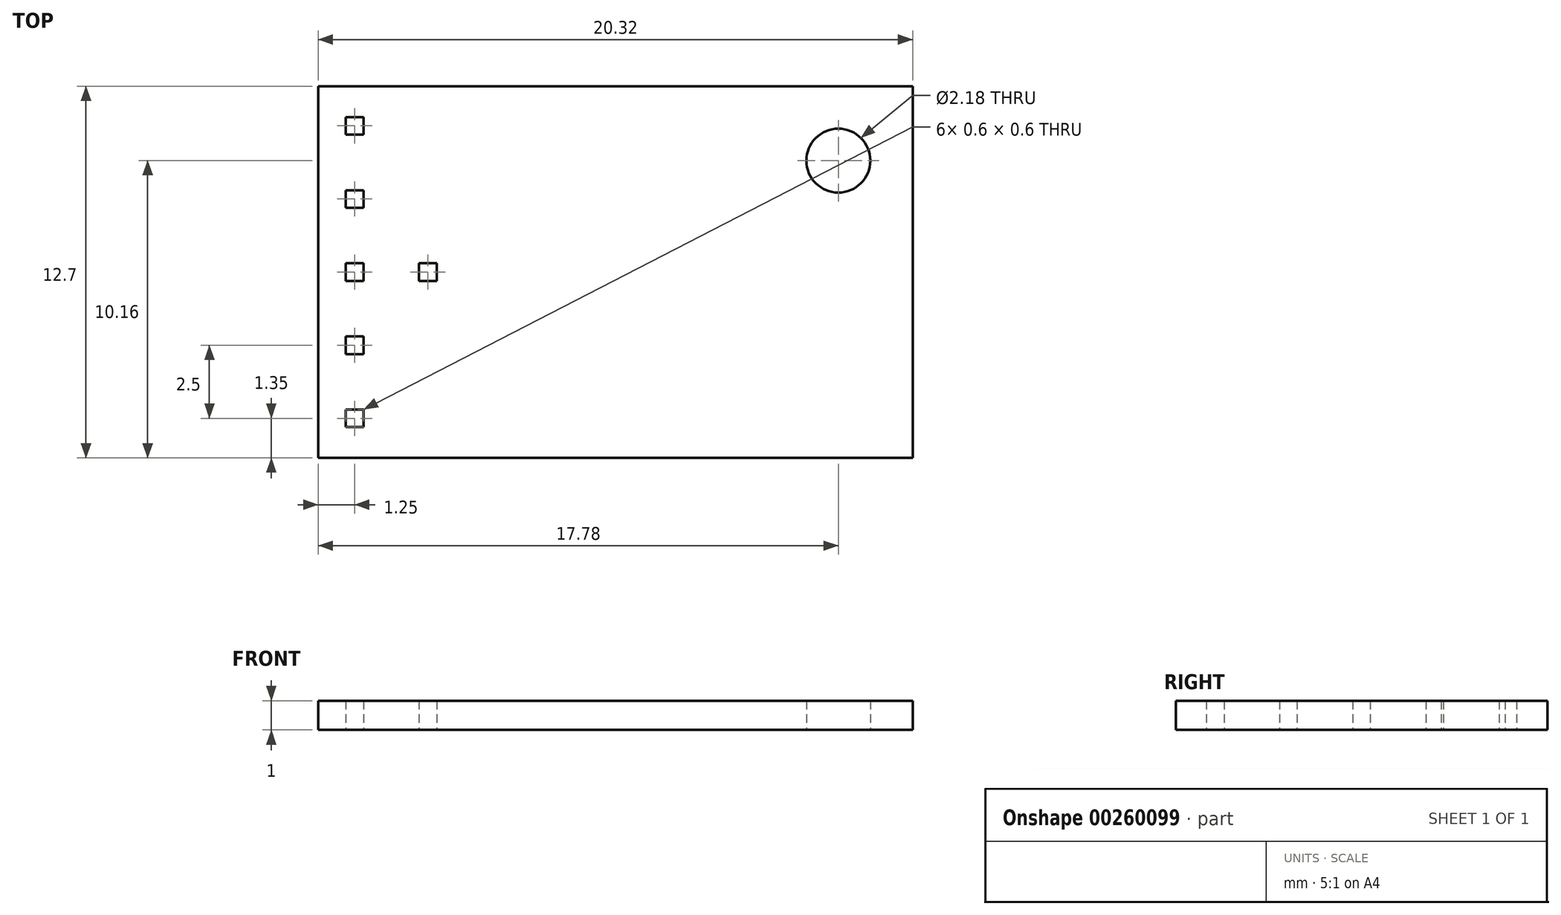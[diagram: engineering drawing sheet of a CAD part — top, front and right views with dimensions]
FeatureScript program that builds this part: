
annotation { "Feature Type Name" : "Feature", "Feature Type Description" : "" }
export const myFeature = defineFeature(function(context is Context, id is Id, definition is map)
    precondition{}
    {
        {
            var Q0;
            Q0=qCreatedBy(makeId("Top.planeOp"),FACE);
            var sketch = newSketch(context, id + "F0", { "sketchPlane" : qUnion([Q0])});
            skLineSegment(sketch, "E0.bottom", {"start": v(0, 0) * mm, "end": v(20.32, 0) * mm});
            skLineSegment(sketch, "E0.top", {"start": v(0, 12.7) * mm, "end": v(20.32, 12.7) * mm});
            skLineSegment(sketch, "E0.left", {"start": v(0, 0) * mm, "end": v(0, 12.7) * mm});
            skLineSegment(sketch, "E0.right", {"start": v(20.32, 0) * mm, "end": v(20.32, 12.7) * mm});
            skCircle(sketch, "E1", {"center": v(17.78, 10.16) * mm, "radius": 1.1 * mm});
            skLineSegment(sketch, "E2", {"start": v(1.25, 12.7) * mm, "end": v(1.25, 0) * mm, "construction": true});
            skLineSegment(sketch, "E3", {"start": v(0, 6.35) * mm, "end": v(20.32, 6.35) * mm, "construction": true});
            skLineSegment(sketch, "E4.bottom", {"start": v(0.95, 6.65) * mm, "end": v(1.55, 6.65) * mm});
            skLineSegment(sketch, "E4.top", {"start": v(0.95, 6.05) * mm, "end": v(1.55, 6.05) * mm});
            skLineSegment(sketch, "E4.left", {"start": v(0.95, 6.65) * mm, "end": v(0.95, 6.05) * mm});
            skLineSegment(sketch, "E4.right", {"start": v(1.55, 6.65) * mm, "end": v(1.55, 6.05) * mm});
            skLineSegment(sketch, "E5.1.0.0", {"start": v(1.55, 9.15) * mm, "end": v(1.55, 8.55) * mm});
            skLineSegment(sketch, "E5.1.0.1", {"start": v(0.95, 9.15) * mm, "end": v(1.55, 9.15) * mm});
            skLineSegment(sketch, "E5.1.0.2", {"start": v(0.95, 9.15) * mm, "end": v(0.95, 8.55) * mm});
            skLineSegment(sketch, "E5.1.0.3", {"start": v(0.95, 8.55) * mm, "end": v(1.55, 8.55) * mm});
            skLineSegment(sketch, "E5.2.0.0", {"start": v(1.55, 11.65) * mm, "end": v(1.55, 11.05) * mm});
            skLineSegment(sketch, "E5.2.0.1", {"start": v(0.95, 11.65) * mm, "end": v(1.55, 11.65) * mm});
            skLineSegment(sketch, "E5.2.0.2", {"start": v(0.95, 11.65) * mm, "end": v(0.95, 11.05) * mm});
            skLineSegment(sketch, "E5.2.0.3", {"start": v(0.95, 11.05) * mm, "end": v(1.55, 11.05) * mm});
            skLineSegment(sketch, "E5.direction1", {"start": v(1.55, 6.05) * mm, "end": v(1.55, 8.55) * mm, "construction": true});
            skLineSegment(sketch, "E6.1.0.0", {"start": v(0.95, 4.15) * mm, "end": v(1.55, 4.15) * mm});
            skLineSegment(sketch, "E6.1.0.1", {"start": v(0.95, 4.15) * mm, "end": v(0.95, 3.55) * mm});
            skLineSegment(sketch, "E6.1.0.2", {"start": v(0.95, 3.55) * mm, "end": v(1.55, 3.55) * mm});
            skLineSegment(sketch, "E6.2.0.0", {"start": v(0.95, 1.65) * mm, "end": v(1.55, 1.65) * mm});
            skLineSegment(sketch, "E6.2.0.1", {"start": v(0.95, 1.65) * mm, "end": v(0.95, 1.05) * mm});
            skLineSegment(sketch, "E6.2.0.2", {"start": v(0.95, 1.05) * mm, "end": v(1.55, 1.05) * mm});
            skLineSegment(sketch, "E6.direction1", {"start": v(0.95, 6.65) * mm, "end": v(0.95, 4.15) * mm, "construction": true});
            skLineSegment(sketch, "E7", {"start": v(1.55, 4.15) * mm, "end": v(1.55, 3.55) * mm});
            skLineSegment(sketch, "E8", {"start": v(1.55, 1.65) * mm, "end": v(1.55, 1.05) * mm});
            skLineSegment(sketch, "E9.bottom", {"start": v(3.45, 6.65) * mm, "end": v(4.05, 6.65) * mm});
            skLineSegment(sketch, "E9.top", {"start": v(3.45, 6.05) * mm, "end": v(4.05, 6.05) * mm});
            skLineSegment(sketch, "E9.left", {"start": v(3.45, 6.65) * mm, "end": v(3.45, 6.05) * mm});
            skLineSegment(sketch, "E9.right", {"start": v(4.05, 6.65) * mm, "end": v(4.05, 6.05) * mm});
            skSolve(sketch);
        }
        {
            var Q0;
            Q0 = qSketchRegion(id + "F0", true);
            extrude(context, id + "F1", {"entities" : qUnion([Q0]), "depth" : 1 * mm});
        }
    });
